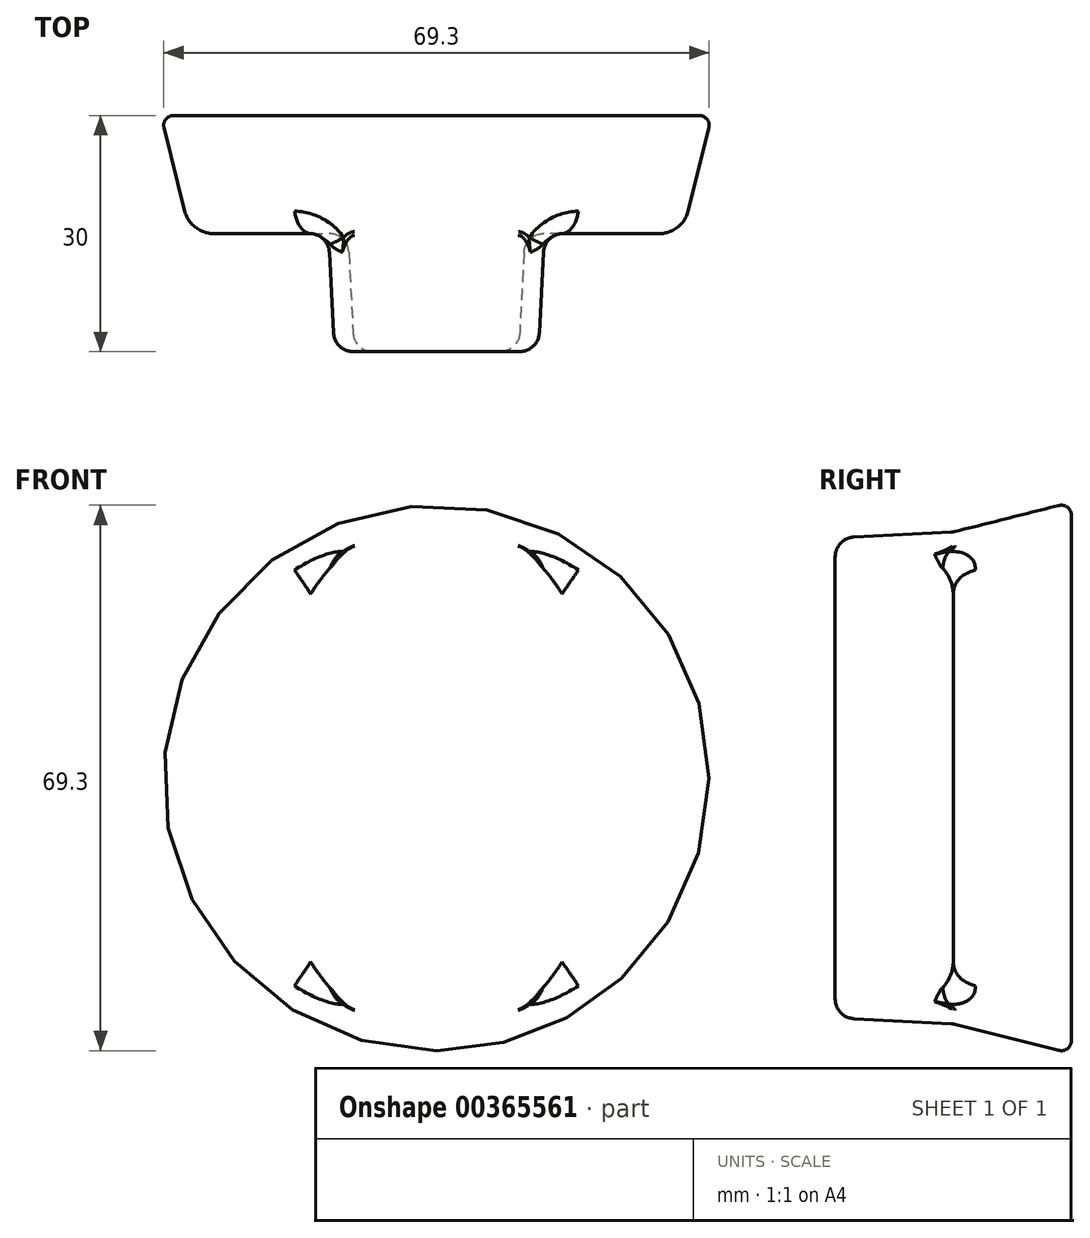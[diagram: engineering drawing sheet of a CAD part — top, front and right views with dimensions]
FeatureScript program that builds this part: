
annotation { "Feature Type Name" : "Feature", "Feature Type Description" : "" }
export const myFeature = defineFeature(function(context is Context, id is Id, definition is map)
    precondition{}
    {
        {
            var Q0;
            Q0=qCreatedBy(makeId("Front.planeOp"),FACE);
            var sketch = newSketch(context, id + "F0", { "sketchPlane" : qUnion([Q0])});
            skCircle(sketch, "E0", {"center": v(0, 0) * mm, "radius": 35 * mm});
            skSolve(sketch);
        }
        {
            var Q0;
            Q0=qCreatedBy(makeId("Front.planeOp"),FACE);
            cPlane(context, id + "F1", {"entities" : qUnion([Q0]), "cplaneType" : CPlaneType.OFFSET, "offset" : 15 * mm, "width" : 152.4 * mm, "height" : 152.4 * mm});
        }
        {
            var Q0;
            Q0=qCreatedBy(id+"F1.planeOp",FACE);
            var sketch = newSketch(context, id + "F2", { "sketchPlane" : qUnion([Q0])});
            skCircle(sketch, "E1", {"center": v(0, 0) * mm, "radius": 31.25 * mm});
            skSolve(sketch);
        }
        {
            var Q0;
            Q0=makeQuery(id+"F0.imprint","IMPRINT",FACE,{"disambiguationData":[TD([[makeQuery(id+"F0.imprint","IMPRINT",EDGE,{"derivedFrom":sQuery(id+"F0.wireOp",EDGE,"E0")}),1.0]])]});
            var Q1;
            Q1=makeQuery(id+"F2.imprint","IMPRINT",FACE,{"disambiguationData":[TD([[makeQuery(id+"F2.imprint","IMPRINT",EDGE,{"derivedFrom":sQuery(id+"F2.wireOp",EDGE,"E1")}),1.0]])]});
            loft(context, id + "F3", {"sheetProfilesArray" : [{ "sheetProfileEntities" : qUnion([Q0]) }, { "sheetProfileEntities" : qUnion([Q1]) }]});
        }
        {
            var Q0;
            Q0=makeQuery(id+"F3.opLoft","CAP_FACE",FACE,{"disambiguationData":[OSD([makeQuery(id+"F2.imprint","IMPRINT",FACE,{"disambiguationData":[TD([[makeQuery(id+"F2.imprint","IMPRINT",EDGE,{"derivedFrom":sQuery(id+"F2.wireOp",EDGE,"E1")}),1.0]])]})])],"isStart":true});
            var sketch = newSketch(context, id + "F4", { "sketchPlane" : qUnion([Q0])});
            skArc(sketch, "E2", {"start": v(-13.63, -23.77) * mm, "mid": v(-11.25, 0) * mm, "end": v(-13.63, 23.77) * mm});
            skArc(sketch, "E3", {"start": v(13.63, 23.77) * mm, "mid": v(11.25, 0) * mm, "end": v(13.63, -23.77) * mm});
            skLineSegment(sketch, "E4", {"start": v(-11.25, 0) * mm, "end": v(11.25, 0) * mm, "construction": true});
            skPoint(sketch, "E5", {"position": v(0, 0) * mm});
            skArc(sketch, "E6.0", {"start": v(-10.39, -29.47) * mm, "mid": v(0, -31.25) * mm, "end": v(10.39, -29.47) * mm});
            skArc(sketch, "E7.trimOffspring", {"start": v(10.39, 29.47) * mm, "mid": v(0, 31.25) * mm, "end": v(-10.39, 29.47) * mm});
            skPoint(sketch, "E8.visualSharp", {"position": v(-14.49, 27.69) * mm});
            skArc(sketch, "E8.filletArc", {"start": v(-10.39, 29.47) * mm, "mid": v(-13.07, 27.23) * mm, "end": v(-13.63, 23.77) * mm});
            skPoint(sketch, "E9.visualSharp", {"position": v(14.49, 27.69) * mm});
            skArc(sketch, "E9.filletArc", {"start": v(13.63, 23.77) * mm, "mid": v(13.07, 27.23) * mm, "end": v(10.39, 29.47) * mm});
            skPoint(sketch, "E10.visualSharp", {"position": v(14.49, -27.69) * mm});
            skArc(sketch, "E10.filletArc", {"start": v(10.39, -29.47) * mm, "mid": v(13.07, -27.23) * mm, "end": v(13.63, -23.77) * mm});
            skPoint(sketch, "E11.visualSharp", {"position": v(-14.49, -27.69) * mm});
            skArc(sketch, "E11.filletArc", {"start": v(-13.63, -23.77) * mm, "mid": v(-13.07, -27.23) * mm, "end": v(-10.39, -29.47) * mm});
            skSolve(sketch);
        }
        {
            var Q0;
            Q0=makeQuery(id+"F4.imprint","IMPRINT",FACE,{"disambiguationData":[TD([[makeQuery(id+"F4.imprint","IMPRINT",EDGE,{"derivedFrom":sQuery(id+"F4.wireOp",EDGE,"E2")}),-1.0]])]});
            extrude(context, id + "F5", {"entities" : qUnion([Q0]), "operationType" : NewBodyOperationType.ADD, "depth" : 15 * mm, "hasDraft" : true, "draftAngle" : 3 * degree, "draftPullDirection" : true});
        }
        {
            var Q0;
            Q0=makeQuery(id+"F5.opExtrude","CAP_EDGE",EDGE,{"disambiguationData":[OSD([sQuery(id+"F4.wireOp",EDGE,"E2")])],"isStart":true});
            var Q1;
            Q1=makeQuery(id+"F5.opExtrude","CAP_EDGE",EDGE,{"disambiguationData":[OSD([sQuery(id+"F4.wireOp",EDGE,"E11.filletArc")])],"isStart":true});
            var Q2;
            Q2=makeQuery(id+"F5.boolean.opBoolean","MERGE",EDGE,{"derivedFrom":[makeQuery(id+"F3.opLoft","MID_CAP_EDGE",EDGE,{"disambiguationData":[OSD([sQuery(id+"F0.wireOp",EDGE,"E0"),sQuery(id+"F2.wireOp",EDGE,"E1")])],"capPos":1.0}),makeQuery(id+"F5.opExtrude","CAP_EDGE",EDGE,{"disambiguationData":[OSD([sQuery(id+"F4.wireOp",EDGE,"E6.0")])],"isStart":true})]});
            var Q3;
            Q3=makeQuery(id+"F5.opExtrude","CAP_EDGE",EDGE,{"disambiguationData":[OSD([sQuery(id+"F4.wireOp",EDGE,"E10.filletArc")])],"isStart":true});
            var Q4;
            Q4=makeQuery(id+"F5.opExtrude","CAP_EDGE",EDGE,{"disambiguationData":[OSD([sQuery(id+"F4.wireOp",EDGE,"E3")])],"isStart":true});
            var Q5;
            Q5=makeQuery(id+"F5.opExtrude","CAP_EDGE",EDGE,{"disambiguationData":[OSD([sQuery(id+"F4.wireOp",EDGE,"E9.filletArc")])],"isStart":true});
            var Q6;
            Q6=makeQuery(id+"F5.boolean.opBoolean","MERGE",EDGE,{"derivedFrom":[makeQuery(id+"F3.opLoft","MID_CAP_EDGE",EDGE,{"disambiguationData":[OSD([sQuery(id+"F0.wireOp",EDGE,"E0"),sQuery(id+"F2.wireOp",EDGE,"E1")])],"capPos":1.0}),makeQuery(id+"F5.opExtrude","CAP_EDGE",EDGE,{"disambiguationData":[OSD([sQuery(id+"F4.wireOp",EDGE,"E7.trimOffspring")])],"isStart":true})]});
            var Q7;
            Q7=makeQuery(id+"F5.opExtrude","CAP_EDGE",EDGE,{"disambiguationData":[OSD([sQuery(id+"F4.wireOp",EDGE,"E8.filletArc")])],"isStart":true});
            fillet(context, id + "F6", {"entities" : qUnion([Q0, Q1, Q2, Q3, Q4, Q5, Q6, Q7]), "radius" : 2.5 * mm, "tangentPropagation" : true, "allowEdgeOverflow" : false});
        }
        {
            var Q0;
            {var subQ0=sQuery(id+"F2.wireOp",EDGE,"E1");var subQ1=sQuery(id+"F0.wireOp",EDGE,"E0");Q0=makeQuery(id+"F5.boolean.opBoolean","SPLIT",EDGE,{"disambiguationData":[TD([makeQuery(id+"F5.opExtrude","SWEPT_FACE",FACE,{"disambiguationData":[OSD([sQuery(id+"F4.wireOp",EDGE,"E9.filletArc")])]})])],"derivedFrom":makeQuery(id+"F3.opLoft","MID_CAP_EDGE",EDGE,{"disambiguationData":[OSD([subQ1,subQ0])],"capPos":1.0})});}
            var Q1;
            {var subQ0=sQuery(id+"F2.wireOp",EDGE,"E1");var subQ1=sQuery(id+"F0.wireOp",EDGE,"E0");Q1=makeQuery(id+"F5.boolean.opBoolean","SPLIT",EDGE,{"disambiguationData":[TD([makeQuery(id+"F5.opExtrude","SWEPT_FACE",FACE,{"disambiguationData":[OSD([sQuery(id+"F4.wireOp",EDGE,"E8.filletArc")])]})])],"derivedFrom":makeQuery(id+"F3.opLoft","MID_CAP_EDGE",EDGE,{"disambiguationData":[OSD([subQ1,subQ0])],"capPos":1.0})});}
            fillet(context, id + "F7", {"entities" : qUnion([Q0, Q1]), "radius" : 3.75 * mm, "tangentPropagation" : true, "allowEdgeOverflow" : false});
        }
        {
            var Q0;
            Q0=makeQuery(id+"F5.opExtrude","CAP_FACE",FACE,{"disambiguationData":[OSD([sQuery(id+"F4.wireOp",EDGE,"E2"),sQuery(id+"F4.wireOp",EDGE,"E3"),sQuery(id+"F4.wireOp",EDGE,"E6.0"),sQuery(id+"F4.wireOp",EDGE,"E7.trimOffspring"),sQuery(id+"F4.wireOp",EDGE,"E8.filletArc"),sQuery(id+"F4.wireOp",EDGE,"E9.filletArc"),sQuery(id+"F4.wireOp",EDGE,"E10.filletArc"),sQuery(id+"F4.wireOp",EDGE,"E11.filletArc")])],"isStart":false});
            fillet(context, id + "F8", {"entities" : qUnion([Q0]), "radius" : 2.5 * mm, "tangentPropagation" : true, "allowEdgeOverflow" : false});
        }
        {
            var Q0;
            Q0=makeQuery(id+"F3.opLoft","MID_CAP_EDGE",EDGE,{"disambiguationData":[OSD([sQuery(id+"F0.wireOp",EDGE,"E0")])],"capPos":0.0});
            fillet(context, id + "F9", {"entities" : qUnion([Q0]), "radius" : 1.25 * mm, "tangentPropagation" : true, "allowEdgeOverflow" : false});
        }
    });
